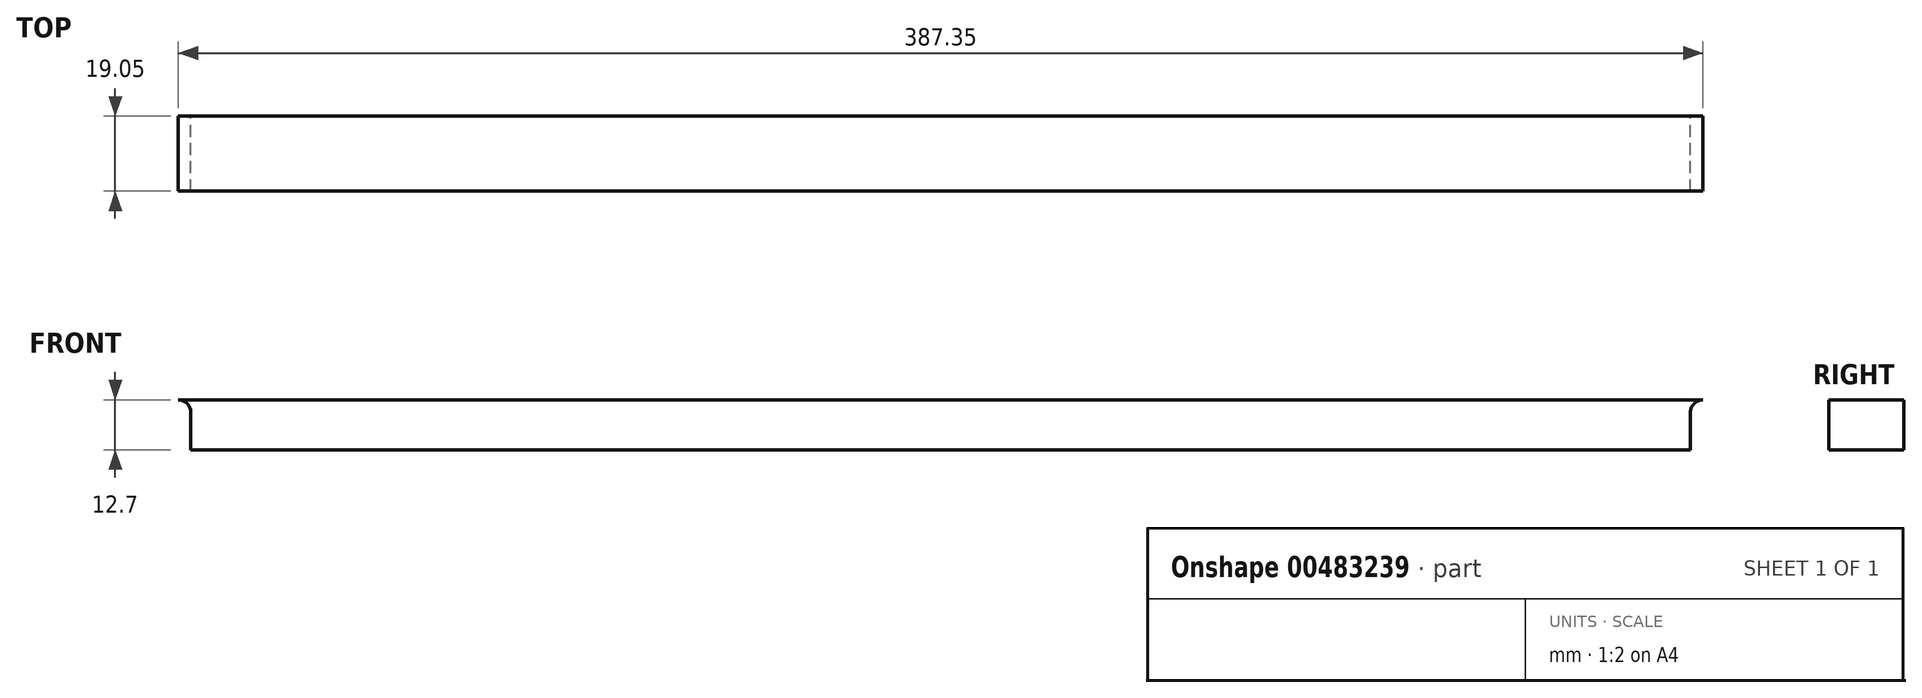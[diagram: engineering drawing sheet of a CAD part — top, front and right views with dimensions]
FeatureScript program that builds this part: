
annotation { "Feature Type Name" : "Feature", "Feature Type Description" : "" }
export const myFeature = defineFeature(function(context is Context, id is Id, definition is map)
    precondition{}
    {
        {
            var Q0;
            Q0=qCreatedBy(makeId("Front.planeOp"),FACE);
            var sketch = newSketch(context, id + "F0", { "sketchPlane" : qUnion([Q0])});
            skLineSegment(sketch, "E0.bottom", {"start": v(118.56, 6.35) * mm, "end": v(-268.79, 6.35) * mm});
            skLineSegment(sketch, "E0.top", {"start": v(115.39, -6.35) * mm, "end": v(-265.61, -6.35) * mm});
            skPoint(sketch, "E0.middle", {"position": v(0, 0) * mm});
            skLineSegment(sketch, "E1", {"start": v(-265.61, 3.17) * mm, "end": v(-265.61, -6.35) * mm});
            skLineSegment(sketch, "E2", {"start": v(115.39, 3.17) * mm, "end": v(115.39, -6.35) * mm});
            skArc(sketch, "E3", {"start": v(118.56, 6.35) * mm, "mid": v(116.32, 5.42) * mm, "end": v(115.39, 3.17) * mm});
            skPoint(sketch, "E4.orphan", {"position": v(268.79, -6.35) * mm});
            skArc(sketch, "E5", {"start": v(-265.61, 3.17) * mm, "mid": v(-266.54, 5.42) * mm, "end": v(-268.79, 6.35) * mm});
            skPoint(sketch, "E6.orphan", {"position": v(-118.56, -6.35) * mm});
            skSolve(sketch);
        }
        {
            var Q0;
            Q0=qSketchRegion(id+"F0",true);
            extrude(context, id + "F1", {"entities" : qUnion([Q0]), "depth" : 19.05 * mm});
        }
    });
